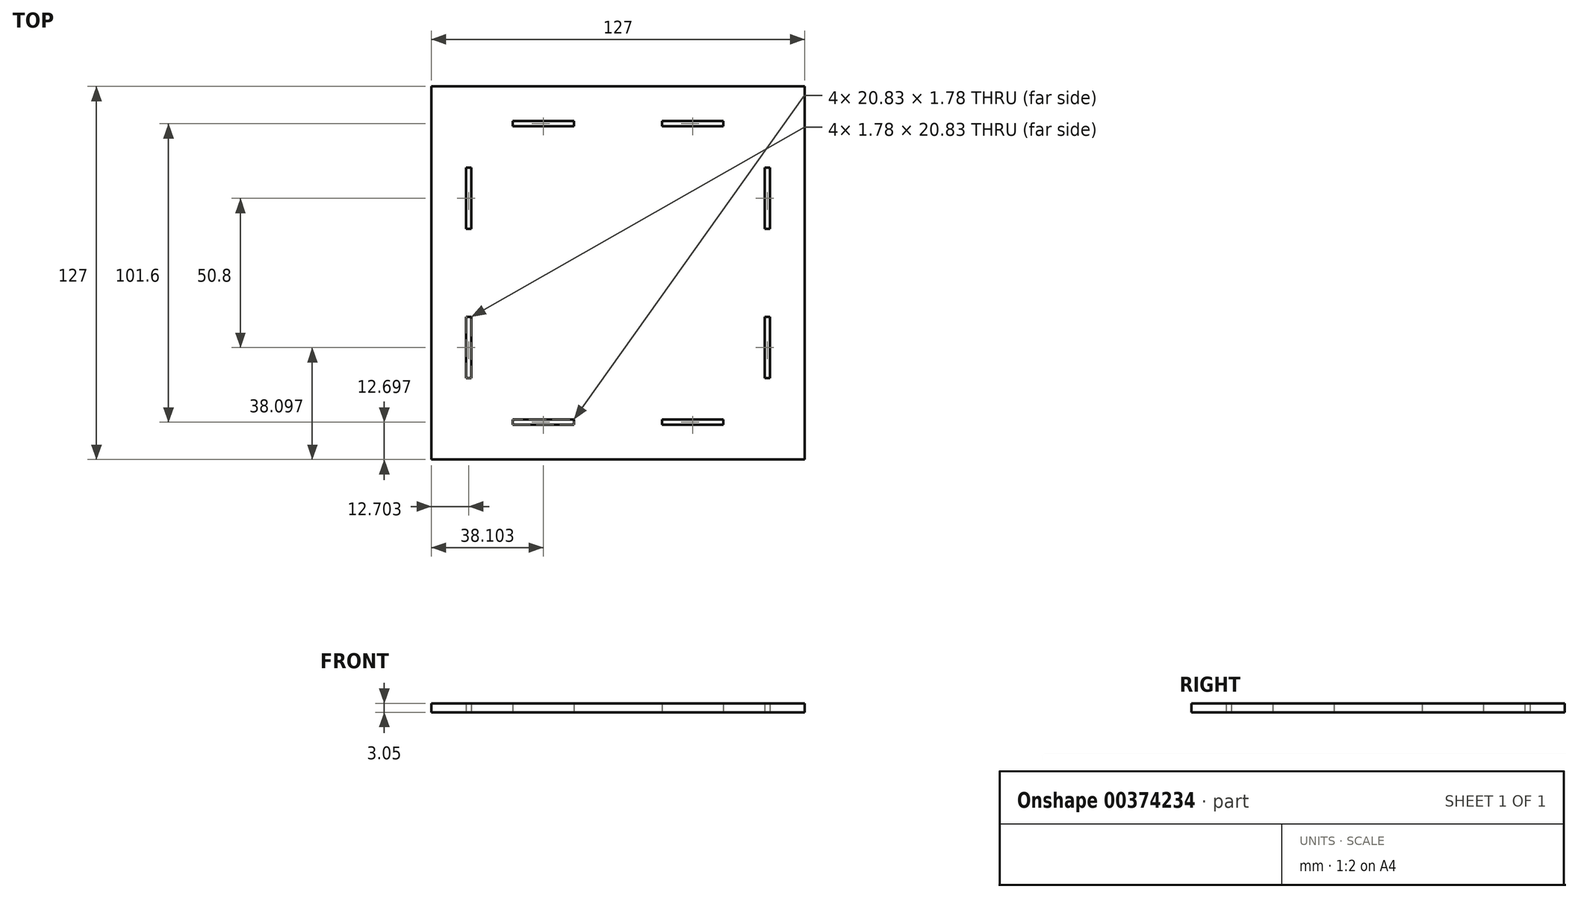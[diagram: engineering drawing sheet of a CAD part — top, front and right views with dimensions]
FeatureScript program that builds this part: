
annotation { "Feature Type Name" : "Feature", "Feature Type Description" : "" }
export const myFeature = defineFeature(function(context is Context, id is Id, definition is map)
    precondition{}
    {
        {
            var Q0;
            Q0=qCreatedBy(makeId("Top.planeOp"),FACE);
            var sketch = newSketch(context, id + "F0", { "sketchPlane" : qUnion([Q0])});
            skLineSegment(sketch, "E0", {"start": v(-335.39, -61.91) * mm, "end": v(-208.39, -61.91) * mm});
            skLineSegment(sketch, "E1", {"start": v(-208.39, -61.91) * mm, "end": v(-208.39, 65.09) * mm});
            skLineSegment(sketch, "E2", {"start": v(-208.39, 65.09) * mm, "end": v(-335.39, 65.09) * mm});
            skLineSegment(sketch, "E3", {"start": v(-335.39, 65.09) * mm, "end": v(-335.39, -61.91) * mm});
            skLineSegment(sketch, "E4", {"start": v(-307.7, 51.5) * mm, "end": v(-286.87, 51.5) * mm, "construction": true});
            skLineSegment(sketch, "E5", {"start": v(-286.87, 51.5) * mm, "end": v(-286.87, 53.28) * mm, "construction": true});
            skLineSegment(sketch, "E6", {"start": v(-286.87, 53.28) * mm, "end": v(-307.7, 53.28) * mm, "construction": true});
            skLineSegment(sketch, "E7", {"start": v(-307.7, 53.28) * mm, "end": v(-307.7, 51.5) * mm, "construction": true});
            skLineSegment(sketch, "E8", {"start": v(-256.9, 51.5) * mm, "end": v(-236.07, 51.5) * mm, "construction": true});
            skLineSegment(sketch, "E9", {"start": v(-236.07, 51.5) * mm, "end": v(-236.07, 53.28) * mm, "construction": true});
            skLineSegment(sketch, "E10", {"start": v(-236.07, 53.28) * mm, "end": v(-256.9, 53.28) * mm, "construction": true});
            skLineSegment(sketch, "E11", {"start": v(-256.9, 53.28) * mm, "end": v(-256.9, 51.5) * mm, "construction": true});
            skLineSegment(sketch, "E12", {"start": v(-307.7, -48.32) * mm, "end": v(-286.87, -48.32) * mm, "construction": true});
            skLineSegment(sketch, "E13", {"start": v(-286.87, -48.32) * mm, "end": v(-286.87, -50.1) * mm, "construction": true});
            skLineSegment(sketch, "E14", {"start": v(-286.87, -50.1) * mm, "end": v(-307.7, -50.1) * mm, "construction": true});
            skLineSegment(sketch, "E15", {"start": v(-307.7, -50.1) * mm, "end": v(-307.7, -48.32) * mm, "construction": true});
            skLineSegment(sketch, "E16", {"start": v(-256.9, -48.32) * mm, "end": v(-236.07, -48.32) * mm, "construction": true});
            skLineSegment(sketch, "E17", {"start": v(-236.07, -48.32) * mm, "end": v(-236.07, -50.1) * mm, "construction": true});
            skLineSegment(sketch, "E18", {"start": v(-236.07, -50.1) * mm, "end": v(-256.9, -50.1) * mm, "construction": true});
            skLineSegment(sketch, "E19", {"start": v(-256.9, -50.1) * mm, "end": v(-256.9, -48.32) * mm, "construction": true});
            skLineSegment(sketch, "E20", {"start": v(-323.58, -34.23) * mm, "end": v(-321.8, -34.23) * mm, "construction": true});
            skLineSegment(sketch, "E21", {"start": v(-321.8, -34.23) * mm, "end": v(-321.8, -13.4) * mm, "construction": true});
            skLineSegment(sketch, "E22", {"start": v(-321.8, -13.4) * mm, "end": v(-323.58, -13.4) * mm, "construction": true});
            skLineSegment(sketch, "E23", {"start": v(-323.58, -13.4) * mm, "end": v(-323.58, -34.23) * mm, "construction": true});
            skLineSegment(sketch, "E24", {"start": v(-220.2, -34.23) * mm, "end": v(-221.98, -34.23) * mm, "construction": true});
            skLineSegment(sketch, "E25", {"start": v(-221.98, -34.23) * mm, "end": v(-221.98, -13.4) * mm, "construction": true});
            skLineSegment(sketch, "E26", {"start": v(-221.98, -13.4) * mm, "end": v(-220.2, -13.4) * mm, "construction": true});
            skLineSegment(sketch, "E27", {"start": v(-220.2, -13.4) * mm, "end": v(-220.2, -34.23) * mm, "construction": true});
            skLineSegment(sketch, "E28", {"start": v(-220.2, 37.4) * mm, "end": v(-221.98, 37.4) * mm, "construction": true});
            skLineSegment(sketch, "E29", {"start": v(-221.98, 37.4) * mm, "end": v(-221.98, 16.57) * mm, "construction": true});
            skLineSegment(sketch, "E30", {"start": v(-221.98, 16.57) * mm, "end": v(-220.2, 16.57) * mm, "construction": true});
            skLineSegment(sketch, "E31", {"start": v(-220.2, 16.57) * mm, "end": v(-220.2, 37.4) * mm, "construction": true});
            skLineSegment(sketch, "E32.bottom", {"start": v(-323.58, 37.4) * mm, "end": v(-321.8, 37.4) * mm});
            skLineSegment(sketch, "E32.top", {"start": v(-323.58, 16.57) * mm, "end": v(-321.8, 16.57) * mm});
            skLineSegment(sketch, "E32.left", {"start": v(-323.58, 37.4) * mm, "end": v(-323.58, 16.57) * mm});
            skLineSegment(sketch, "E32.right", {"start": v(-321.8, 37.4) * mm, "end": v(-321.8, 16.57) * mm});
            skLineSegment(sketch, "E33.bottom", {"start": v(-323.58, -13.4) * mm, "end": v(-321.8, -13.4) * mm});
            skLineSegment(sketch, "E33.top", {"start": v(-323.58, -34.23) * mm, "end": v(-321.8, -34.23) * mm});
            skLineSegment(sketch, "E33.left", {"start": v(-323.58, -13.4) * mm, "end": v(-323.58, -34.23) * mm});
            skLineSegment(sketch, "E33.right", {"start": v(-321.8, -13.4) * mm, "end": v(-321.8, -34.23) * mm});
            skLineSegment(sketch, "E34.bottom", {"start": v(-307.7, -48.32) * mm, "end": v(-286.87, -48.32) * mm});
            skLineSegment(sketch, "E34.top", {"start": v(-307.7, -50.1) * mm, "end": v(-286.87, -50.1) * mm});
            skLineSegment(sketch, "E34.left", {"start": v(-307.7, -48.32) * mm, "end": v(-307.7, -50.1) * mm});
            skLineSegment(sketch, "E34.right", {"start": v(-286.87, -48.32) * mm, "end": v(-286.87, -50.1) * mm});
            skLineSegment(sketch, "E35.bottom", {"start": v(-256.9, -48.32) * mm, "end": v(-236.07, -48.32) * mm});
            skLineSegment(sketch, "E35.top", {"start": v(-256.9, -50.1) * mm, "end": v(-236.07, -50.1) * mm});
            skLineSegment(sketch, "E35.left", {"start": v(-256.9, -48.32) * mm, "end": v(-256.9, -50.1) * mm});
            skLineSegment(sketch, "E35.right", {"start": v(-236.07, -48.32) * mm, "end": v(-236.07, -50.1) * mm});
            skLineSegment(sketch, "E36.bottom", {"start": v(-221.98, -13.4) * mm, "end": v(-220.2, -13.4) * mm});
            skLineSegment(sketch, "E36.top", {"start": v(-221.98, -34.23) * mm, "end": v(-220.2, -34.23) * mm});
            skLineSegment(sketch, "E36.left", {"start": v(-221.98, -13.4) * mm, "end": v(-221.98, -34.23) * mm});
            skLineSegment(sketch, "E36.right", {"start": v(-220.2, -13.4) * mm, "end": v(-220.2, -34.23) * mm});
            skLineSegment(sketch, "E37.bottom", {"start": v(-221.98, 37.4) * mm, "end": v(-220.2, 37.4) * mm});
            skLineSegment(sketch, "E37.top", {"start": v(-221.98, 16.57) * mm, "end": v(-220.2, 16.57) * mm});
            skLineSegment(sketch, "E37.left", {"start": v(-221.98, 37.4) * mm, "end": v(-221.98, 16.57) * mm});
            skLineSegment(sketch, "E37.right", {"start": v(-220.2, 37.4) * mm, "end": v(-220.2, 16.57) * mm});
            skLineSegment(sketch, "E38.bottom", {"start": v(-256.9, 53.28) * mm, "end": v(-236.07, 53.28) * mm});
            skLineSegment(sketch, "E38.top", {"start": v(-256.9, 51.5) * mm, "end": v(-236.07, 51.5) * mm});
            skLineSegment(sketch, "E38.left", {"start": v(-256.9, 53.28) * mm, "end": v(-256.9, 51.5) * mm});
            skLineSegment(sketch, "E38.right", {"start": v(-236.07, 53.28) * mm, "end": v(-236.07, 51.5) * mm});
            skLineSegment(sketch, "E39.bottom", {"start": v(-307.7, 53.28) * mm, "end": v(-286.87, 53.28) * mm});
            skLineSegment(sketch, "E39.top", {"start": v(-307.7, 51.5) * mm, "end": v(-286.87, 51.5) * mm});
            skLineSegment(sketch, "E39.left", {"start": v(-307.7, 53.28) * mm, "end": v(-307.7, 51.5) * mm});
            skLineSegment(sketch, "E39.right", {"start": v(-286.87, 53.28) * mm, "end": v(-286.87, 51.5) * mm});
            skSolve(sketch);
        }
        {
            var Q0;
            Q0=makeQuery(id+"F0.imprint","IMPRINT",FACE,{"disambiguationData":[TD([[makeQuery(id+"F0.imprint","IMPRINT",EDGE,{"derivedFrom":sQuery(id+"F0.wireOp",EDGE,"E0")}),1.0]])]});
            extrude(context, id + "F1", {"entities" : qUnion([Q0]), "depth" : 3.05 * mm});
        }
    });
